# Revit family: Парковый лежак 2 Арт 9978
name_source: partatom
category: Антураж
revit_build: Autodesk Revit 2018 (Build: 20180423_1000(x64)
units: mm (PartAtom-declared; Revit-internal decimal feet)

## family parameters
Всегда вертикально = Да
Источник визуального образа = Геометрия семейства
На основе рабочей плоскости = Нет
Общий = Нет
При загрузке вырезать с полостями = Нет
Точка расчета площади = Нет

## types (3) — shared parameters
URL = https://hobbyka.ru
Артикул товара = Арт. 9978
Высота = 1058 мм
Группа модели = Лежаки и шезлонги
Изготовитель = ООО «Хоббика»
Изображение типоразмера = Парковый лежак 2 Арт 9978.jpg
Цвет каркаса = Сталь
Цвет сидения = Дерево Тик
Ширина = 1892 мм

## per-type parameters (varying)
| type | Версия 0,7 м | Версия 1,4 м | Версия 1,4 м (композит) | Длина | Материал изделия | Описание |
| Версия 0,7 м | Да | Нет | Нет | 700 мм | Сталь, дерево | Парковый лежак 2 «Версия 0,7 м» |
| Версия 1,4 м | Нет | Да | Нет | 1400 мм | Сталь, дерево | Парковый лежак 2 «Версия 1,4 м» |
| Версия 1,4 м (Композит) | Нет | Нет | Да | 1400 мм | Сталь, ДПК | Парковый лежак 2 «Версия 1,4 м (Композит)» |
